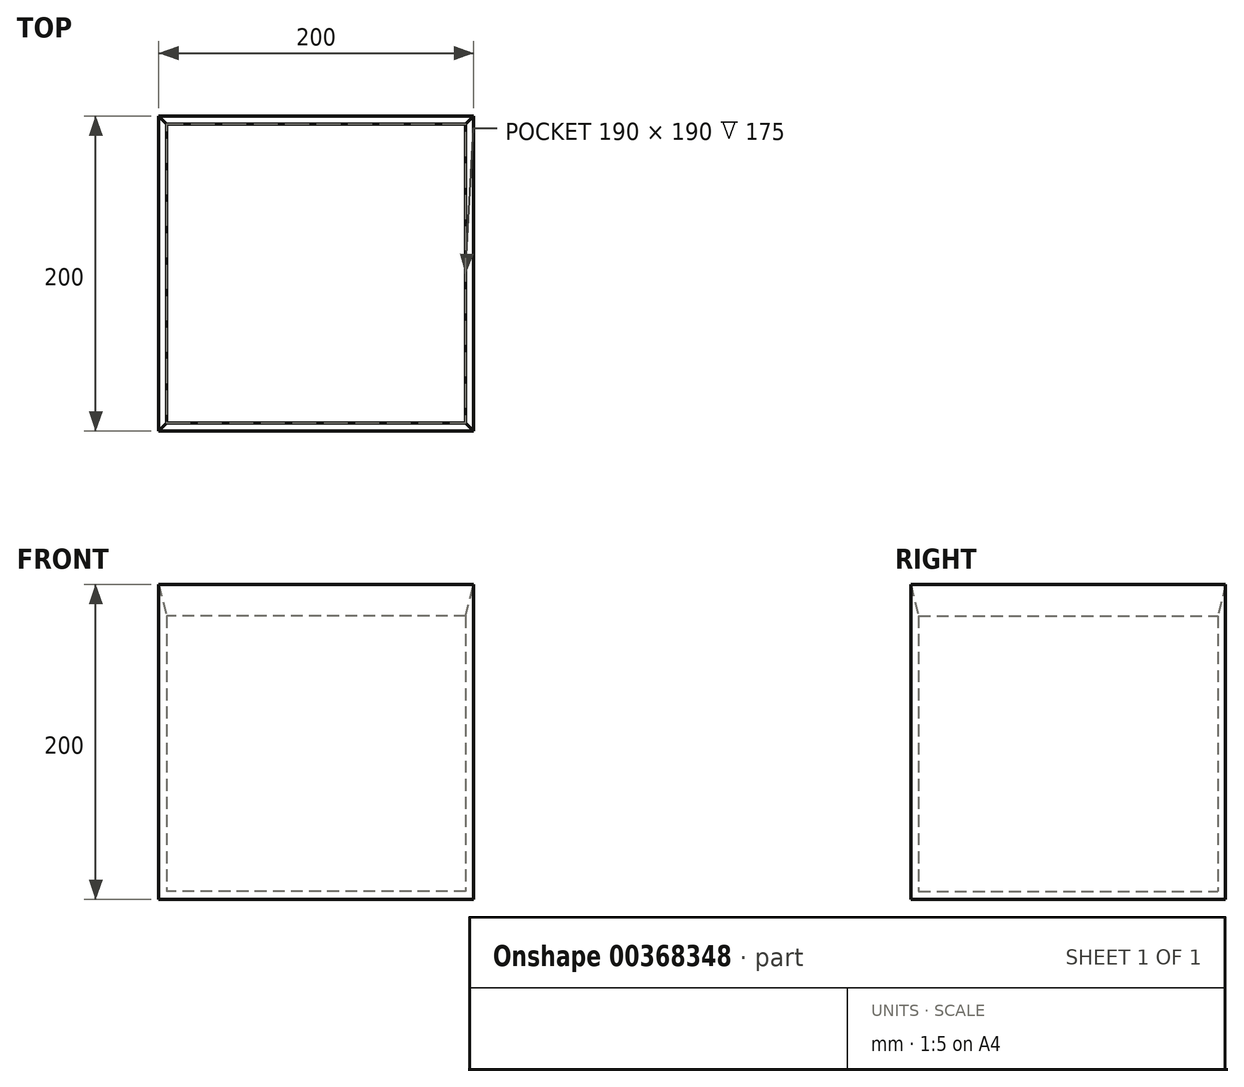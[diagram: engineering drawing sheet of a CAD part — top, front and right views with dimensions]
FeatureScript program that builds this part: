
annotation { "Feature Type Name" : "Feature", "Feature Type Description" : "" }
export const myFeature = defineFeature(function(context is Context, id is Id, definition is map)
    precondition{}
    {
        {
            var Q0;
            Q0=qCreatedBy(makeId("Top.planeOp"),FACE);
            var sketch = newSketch(context, id + "F0", { "sketchPlane" : qUnion([Q0])});
            skLineSegment(sketch, "E0.bottom", {"start": v(100, -100) * mm, "end": v(-100, -100) * mm});
            skLineSegment(sketch, "E0.top", {"start": v(100, 100) * mm, "end": v(-100, 100) * mm});
            skLineSegment(sketch, "E0.left", {"start": v(100, -100) * mm, "end": v(100, 100) * mm});
            skLineSegment(sketch, "E0.right", {"start": v(-100, -100) * mm, "end": v(-100, 100) * mm});
            skPoint(sketch, "E0.middle", {"position": v(0, 0) * mm});
            skLineSegment(sketch, "E1.0", {"start": v(95, 95) * mm, "end": v(-95, 95) * mm});
            skLineSegment(sketch, "E1.1", {"start": v(95, -95) * mm, "end": v(95, 95) * mm});
            skLineSegment(sketch, "E1.2", {"start": v(95, -95) * mm, "end": v(-95, -95) * mm});
            skLineSegment(sketch, "E1.3", {"start": v(-95, -95) * mm, "end": v(-95, 95) * mm});
            skSolve(sketch);
        }
        {
            var Q0;
            {var subQ0=sQuery(id+"F0.wireOp",EDGE,"E1.3");var subQ1=sQuery(id+"F0.wireOp",EDGE,"E1.0");var subQ2=makeQuery(id+"F0.imprint","INTERSECT",VERTEX,{"derivedFrom":[subQ1,subQ0]});Q0=makeQuery(id+"F0.imprint","IMPRINT",FACE,{"disambiguationData":[TD([[makeQuery(id+"F0.imprint","IMPRINT",EDGE,{"disambiguationData":[TD([[subQ2,1.0]])],"derivedFrom":subQ1}),1.0]])]});}
            var Q1;
            {var subQ0=sQuery(id+"F0.wireOp",EDGE,"E1.1");var subQ1=sQuery(id+"F0.wireOp",EDGE,"E1.0");var subQ2=makeQuery(id+"F0.imprint","INTERSECT",VERTEX,{"derivedFrom":[subQ1,subQ0]});Q1=makeQuery(id+"F0.imprint","IMPRINT",FACE,{"disambiguationData":[TD([[makeQuery(id+"F0.imprint","IMPRINT",EDGE,{"disambiguationData":[TD([[subQ2,-1.0]])],"derivedFrom":subQ1}),1.0]])]});}
            var Q2;
            {var subQ0=sQuery(id+"F0.wireOp",EDGE,"E1.2");var subQ1=sQuery(id+"F0.wireOp",EDGE,"E1.1");var subQ2=makeQuery(id+"F0.imprint","INTERSECT",VERTEX,{"derivedFrom":[subQ1,subQ0]});Q2=makeQuery(id+"F0.imprint","IMPRINT",FACE,{"disambiguationData":[TD([[makeQuery(id+"F0.imprint","IMPRINT",EDGE,{"disambiguationData":[TD([[subQ2,-1.0]])],"derivedFrom":subQ1}),1.0]])]});}
            var Q3;
            {var subQ0=sQuery(id+"F0.wireOp",EDGE,"E1.3");var subQ1=sQuery(id+"F0.wireOp",EDGE,"E1.2");var subQ2=makeQuery(id+"F0.imprint","INTERSECT",VERTEX,{"derivedFrom":[subQ1,subQ0]});Q3=makeQuery(id+"F0.imprint","IMPRINT",FACE,{"disambiguationData":[TD([[makeQuery(id+"F0.imprint","IMPRINT",EDGE,{"disambiguationData":[TD([[subQ2,1.0]])],"derivedFrom":subQ1}),-1.0]])]});}
            extrude(context, id + "F1", {"entities" : qUnion([Q0, Q1, Q2, Q3]), "depth" : 5 * mm});
        }
        {
            var Q0;
            Q0=makeQuery(id+"F0.imprint","IMPRINT",FACE,{"disambiguationData":[TD([[makeQuery(id+"F0.imprint","IMPRINT",EDGE,{"derivedFrom":sQuery(id+"F0.wireOp",EDGE,"E0.bottom")}),-1.0]])]});
            extrude(context, id + "F2", {"entities" : qUnion([Q0]), "operationType" : NewBodyOperationType.ADD, "depth" : 200 * mm});
        }
        {
            var Q0;
            Q0=makeQuery(id+"F2.opExtrude","CAP_EDGE",EDGE,{"disambiguationData":[OSD([sQuery(id+"F0.wireOp",EDGE,"E1.3")])],"isStart":false});
            var Q1;
            Q1=makeQuery(id+"F2.opExtrude","CAP_EDGE",EDGE,{"disambiguationData":[OSD([sQuery(id+"F0.wireOp",EDGE,"E1.2")])],"isStart":false});
            var Q2;
            Q2=makeQuery(id+"F2.opExtrude","CAP_EDGE",EDGE,{"disambiguationData":[OSD([sQuery(id+"F0.wireOp",EDGE,"E1.1")])],"isStart":false});
            var Q3;
            Q3=makeQuery(id+"F2.opExtrude","CAP_EDGE",EDGE,{"disambiguationData":[OSD([sQuery(id+"F0.wireOp",EDGE,"E1.0")])],"isStart":false});
            chamfer(context, id + "F3", {"entities" : qUnion([Q0, Q1, Q2, Q3]), "chamferType" : ChamferType.TWO_OFFSETS, "width1" : 5 * mm, "oppositeDirection" : false, "width2" : 20 * mm, "tangentPropagation" : true});
        }
    });
